# Revit family: РИДАН_Автоматический клапан AQT-R3
name_source: partatom
category: Арматура трубопроводов
units: mm (PartAtom-declared; Revit-internal decimal feet)

## family parameters
Всегда вертикально = Да
На основе рабочей плоскости = Нет
Общий = Нет
При загрузке вырезать с полостями = Нет
Размер круглого соединителя = Использовать диаметр
Тип детали = Вставляется

## types (10) — shared parameters
ADSK_Версия Revit = 2019
ADSK_Версия семейства = 1.0
ADSK_Единица измерения = шт.
ADSK_Завод-изготовитель = ООО «Ридан-Трейд»
ADSK_Количество = 1
ADSK_Расход жидкости = 0.0 л/с
LT = AQT-R3
URL = https://ridan.ru
b = 2 мм
Изготовитель = Ридан

## per-type parameters (varying)
| type | ADSK_Диаметр условный | ADSK_Код изделия | ADSK_Марка | ADSK_Масса | ADSK_Наименование | DP | LF_1 | a | c | d | e | f | g | h | nip | Ниппели |
| DN 15 LF с ниппелями | 15 мм | 003Z1811R3 | AQT-R3 LF DN15 | 0.48 | Автоматический комбинированный балансировочный клапан AQT-R3 LF с изм. ниппелями, PN16, Tmax=120C, DN15 | 20 мм | 1 | 6 мм | 51 мм | 24 мм | 4 мм | 26 мм | 23 мм | 67 мм | 1 | Да |
| DN 15 с ниппелями | 15 мм | 003Z1812R3 | AQT-R3 DN15 | 0.48 | Автоматический комбинированный балансировочный клапан AQT-R3 с изм. ниппелями, PN16, Tmax=120C, DN15 | 20 мм | 0 | 6 мм | 51 мм | 24 мм | 4 мм | 26 мм | 23 мм | 67 мм | 1 | Да |
| DN 20 с ниппелями | 20 мм | 003Z1813R3 | AQT-R3 DN20 | 0.65 | Автоматический комбинированный балансировочный клапан AQT-R3 с изм. ниппелями, PN16, Tmax=120C, DN20 | 25 мм | 0 | 8 мм | 64 мм | 31 мм | 5 мм | 33 мм | 30 мм | 84 мм | 1 | Да |
| DN 25 с ниппелями | 25 мм | 003Z1814R3 | AQT-R3 DN25 | 1.45 | Автоматический комбинированный балансировочный клапан AQT-R3 с изм. ниппелями, PN16, Tmax=120C, DN25 | 32 мм | 0 | 10 мм | 82 мм | 40 мм | 6 мм | 42 мм | 39 мм | 106 мм | 1 | Да |
| DN 32 с ниппелями | 32 мм | 003Z1815R3 | AQT-R3 DN32 | 2.21 | Автоматический комбинированный балансировочный клапан AQT-R3 с изм. ниппелями, PN16, Tmax=120C, DN32 | 40 мм | 0 | 12 мм | 103 мм | 51 мм | 7 мм | 48 мм | 44 мм | 130 мм | 1 | Да |
| DN 15 LF без ниппелей | 15 мм | 003Z1801R3 | AQT-R3 LF DN15 | 0.48 | Автоматический комбинированный балансировочный клапан AQT-R3 LF без изм. ниппелей, PN16, Tmax=120C, DN15 | 20 мм | 1 | 6 мм | 51 мм | 24 мм | 4 мм | 26 мм | 23 мм | 67 мм | 0 | Нет |
| DN 20 без ниппелей | 20 мм | 003Z1803R3 | AQT-R3 DN20 | 0.65 | Автоматический комбинированный балансировочный клапан AQT-R3 без изм. ниппелей, PN16, Tmax=120C, DN20 | 25 мм | 0 | 8 мм | 64 мм | 31 мм | 5 мм | 33 мм | 30 мм | 84 мм | 0 | Нет |
| DN 25 без ниппелей | 25 мм | 003Z1804R3 | AQT-R3 DN25 | 1.45 | Автоматический комбинированный балансировочный клапан AQT-R3 без изм. ниппелей, PN16, Tmax=120C, DN25 | 32 мм | 0 | 10 мм | 82 мм | 40 мм | 6 мм | 42 мм | 39 мм | 106 мм | 0 | Нет |
| DN 32 без ниппелей | 32 мм | 003Z1805R3 | AQT-R3 DN32 | 2.21 | Автоматический комбинированный балансировочный клапан AQT-R3 без изм. ниппелей, PN16, Tmax=120C, DN32 | 40 мм | 0 | 12 мм | 103 мм | 51 мм | 7 мм | 48 мм | 44 мм | 130 мм | 0 | Нет |
| DN 15 без ниппелей | 15 мм | 003Z1802R3 | AQT-R3 DN15 | 0.48 | Автоматический комбинированный балансировочный клапан AQT-R3 без изм. ниппелей, PN16, Tmax=120C, DN15 | 20 мм | 0 | 6 мм | 51 мм | 24 мм | 4 мм | 26 мм | 23 мм | 67 мм | 0 | Нет |
